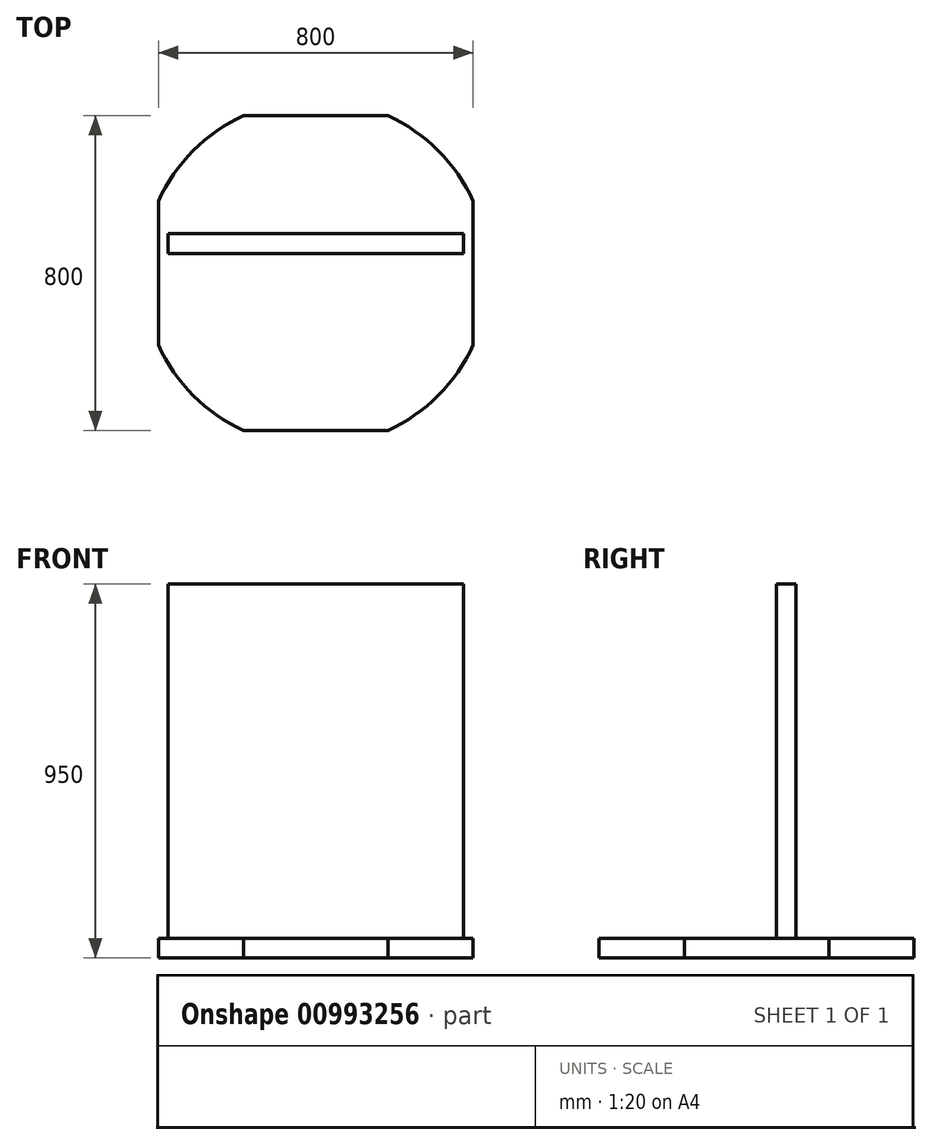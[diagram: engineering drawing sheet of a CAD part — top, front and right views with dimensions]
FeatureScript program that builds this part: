
annotation { "Feature Type Name" : "Feature", "Feature Type Description" : "" }
export const myFeature = defineFeature(function(context is Context, id is Id, definition is map)
    precondition{}
    {
        {
            var Q0;
            Q0=qCreatedBy(makeId("Top.planeOp"),FACE);
            var sketch = newSketch(context, id + "F0", { "sketchPlane" : qUnion([Q0])});
            skLineSegment(sketch, "E0.bottom", {"start": v(400, 400) * mm, "end": v(-400, 400) * mm});
            skLineSegment(sketch, "E0.top", {"start": v(400, -400) * mm, "end": v(-400, -400) * mm});
            skLineSegment(sketch, "E0.left", {"start": v(400, 400) * mm, "end": v(400, -400) * mm});
            skLineSegment(sketch, "E0.right", {"start": v(-400, 400) * mm, "end": v(-400, -400) * mm});
            skPoint(sketch, "E0.middle", {"position": v(0, 0) * mm});
            skCircle(sketch, "E1", {"center": v(0, 0) * mm, "radius": 440 * mm});
            skSolve(sketch);
        }
        {
            var Q0;
            {var subQ0=sQuery(id+"F0.wireOp",EDGE,"E1");var subQ10=sQuery(id+"F0.wireOp",EDGE,"E0.bottom");var subQ11=makeQuery(id+"F0.imprint","INTERSECT",VERTEX,{"disambiguationData":[OD(0.0)],"derivedFrom":[subQ10,subQ0]});Q0=makeQuery(id+"F0.imprint","IMPRINT",FACE,{"disambiguationData":[TD([[makeQuery(id+"F0.imprint","IMPRINT",EDGE,{"disambiguationData":[TD([[subQ11,-1.0]])],"derivedFrom":subQ10}),1.0]])]});}
            extrude(context, id + "F1", {"entities" : qUnion([Q0]), "depth" : 50 * mm, "offsetDistance" : 25 * mm});
        }
        {
            var Q0;
            Q0=makeQuery(id+"F1.opExtrude","CAP_FACE",FACE,{"disambiguationData":[OSD([sQuery(id+"F0.wireOp",EDGE,"E0.bottom"),sQuery(id+"F0.wireOp",EDGE,"E0.top"),sQuery(id+"F0.wireOp",EDGE,"E0.left"),sQuery(id+"F0.wireOp",EDGE,"E0.right"),sQuery(id+"F0.wireOp",EDGE,"E1")])],"isStart":false});
            var sketch = newSketch(context, id + "F2", { "sketchPlane" : qUnion([Q0])});
            skLineSegment(sketch, "E2.bottom", {"start": v(375, 100) * mm, "end": v(-375, 100) * mm});
            skLineSegment(sketch, "E2.top", {"start": v(375, 50) * mm, "end": v(-375, 50) * mm});
            skLineSegment(sketch, "E2.left", {"start": v(375, 100) * mm, "end": v(375, 50) * mm});
            skLineSegment(sketch, "E2.right", {"start": v(-375, 100) * mm, "end": v(-375, 50) * mm});
            skPoint(sketch, "E2.middle", {"position": v(0, 75) * mm});
            skSolve(sketch);
        }
        {
            var Q0;
            Q0=makeQuery(id+"F2.imprint","IMPRINT",FACE,{"disambiguationData":[TD([[makeQuery(id+"F2.imprint","IMPRINT",EDGE,{"derivedFrom":sQuery(id+"F2.wireOp",EDGE,"E2.bottom")}),1.0]])]});
            extrude(context, id + "F3", {"entities" : qUnion([Q0]), "depth" : 900 * mm, "offsetDistance" : 25 * mm});
        }
    });
